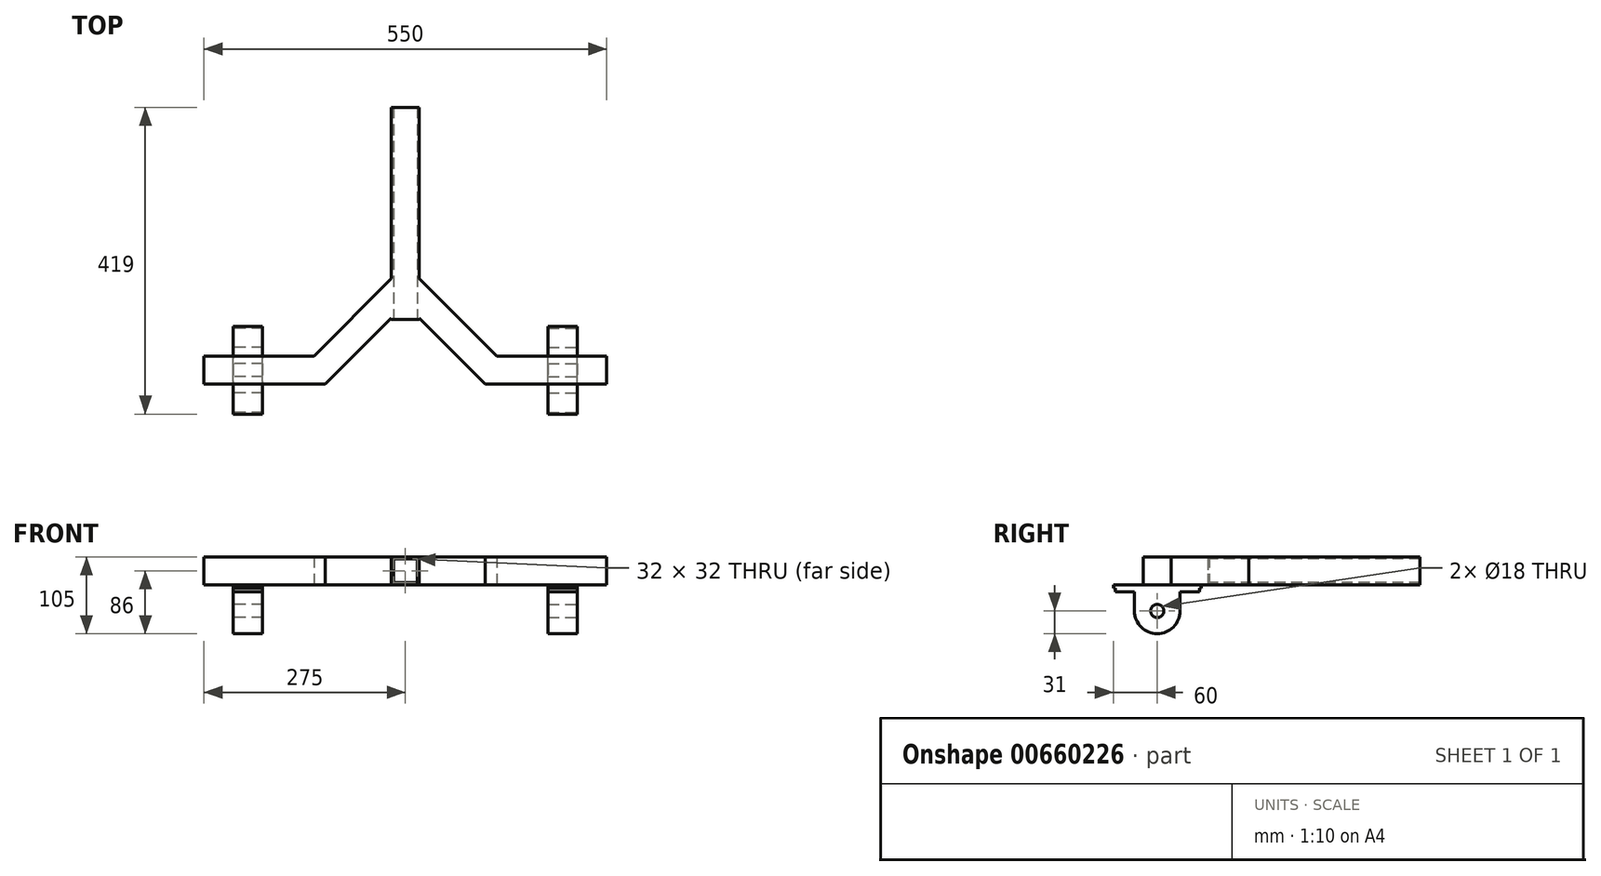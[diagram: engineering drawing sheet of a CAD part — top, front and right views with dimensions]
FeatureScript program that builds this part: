
annotation { "Feature Type Name" : "Feature", "Feature Type Description" : "" }
export const myFeature = defineFeature(function(context is Context, id is Id, definition is map)
    precondition{}
    {
        {
            var Q0;
            Q0=qCreatedBy(makeId("Top.planeOp"),FACE);
            var sketch = newSketch(context, id + "F0", { "sketchPlane" : qUnion([Q0])});
            skLineSegment(sketch, "E0.bottom", {"start": v(-275, -19) * mm, "end": v(-109.26, -19) * mm});
            skLineSegment(sketch, "E0.top", {"start": v(-275, 19) * mm, "end": v(-125, 19) * mm});
            skLineSegment(sketch, "E0.left", {"start": v(-275, -19) * mm, "end": v(-275, 19) * mm});
            skLineSegment(sketch, "E0.right", {"start": v(275, -19) * mm, "end": v(275, 19) * mm});
            skLineSegment(sketch, "E1", {"start": v(-125, 19) * mm, "end": v(-19, 125) * mm});
            skLineSegment(sketch, "E2", {"start": v(125, 19) * mm, "end": v(19, 125) * mm});
            skLineSegment(sketch, "E3", {"start": v(-109.26, -19) * mm, "end": v(-19, 71.26) * mm});
            skLineSegment(sketch, "E4.bottom", {"start": v(-19, 69) * mm, "end": v(19, 69) * mm});
            skLineSegment(sketch, "E4.top", {"start": v(-19, 359) * mm, "end": v(19, 359) * mm});
            skLineSegment(sketch, "E4.left", {"start": v(-19, 69) * mm, "end": v(-19, 71.26) * mm});
            skLineSegment(sketch, "E4.right", {"start": v(19, 69) * mm, "end": v(19, 71.26) * mm});
            skLineSegment(sketch, "E5.trimOffspring", {"start": v(109.26, -19) * mm, "end": v(275, -19) * mm});
            skLineSegment(sketch, "E6.trimOffspring", {"start": v(125, 19) * mm, "end": v(275, 19) * mm});
            skLineSegment(sketch, "E7.trimOffspring", {"start": v(-19, 125) * mm, "end": v(-19, 359) * mm});
            skLineSegment(sketch, "E8.trimOffspring", {"start": v(19, 71.26) * mm, "end": v(109.26, -19) * mm});
            skLineSegment(sketch, "E9.trimOffspring", {"start": v(19, 125) * mm, "end": v(19, 359) * mm});
            skSolve(sketch);
        }
        {
            var Q0;
            Q0 = qSketchRegion(id + "F0", true);
            extrude(context, id + "F1", {"entities" : qUnion([Q0]), "depth" : 38 * mm, "offsetDistance" : 25 * mm});
        }
        {
            var Q0;
            Q0=makeQuery(id+"F1.opExtrude","SWEPT_FACE",FACE,{"disambiguationData":[OSD([sQuery(id+"F0.wireOp",EDGE,"E4.bottom")])]});
            var sketch = newSketch(context, id + "F2", { "sketchPlane" : qUnion([Q0])});
            skLineSegment(sketch, "E10.bottom", {"start": v(-16, 35) * mm, "end": v(16, 35) * mm});
            skLineSegment(sketch, "E10.top", {"start": v(-16, 3) * mm, "end": v(16, 3) * mm});
            skLineSegment(sketch, "E10.left", {"start": v(-16, 35) * mm, "end": v(-16, 3) * mm});
            skLineSegment(sketch, "E10.right", {"start": v(16, 35) * mm, "end": v(16, 3) * mm});
            skSolve(sketch);
        }
        {
            var Q0;
            Q0 = qSketchRegion(id + "F2", true);
            extrude(context, id + "F3", {"entities" : qUnion([Q0]), "operationType" : NewBodyOperationType.REMOVE, "endBound" : BoundingType.THROUGH_ALL, "oppositeDirection" : true, "depth" : 150 * mm, "offsetDistance" : 25 * mm});
        }
        {
            var Q0;
            Q0=makeQuery(id+"F1.opExtrude","CAP_FACE",FACE,{"disambiguationData":[OSD([sQuery(id+"F0.wireOp",EDGE,"E0.bottom"),sQuery(id+"F0.wireOp",EDGE,"E0.top"),sQuery(id+"F0.wireOp",EDGE,"E0.left"),sQuery(id+"F0.wireOp",EDGE,"E0.right"),sQuery(id+"F0.wireOp",EDGE,"E1"),sQuery(id+"F0.wireOp",EDGE,"E2"),sQuery(id+"F0.wireOp",EDGE,"E3"),sQuery(id+"F0.wireOp",EDGE,"E4.bottom"),sQuery(id+"F0.wireOp",EDGE,"E4.top"),sQuery(id+"F0.wireOp",EDGE,"E4.left"),sQuery(id+"F0.wireOp",EDGE,"E4.right"),sQuery(id+"F0.wireOp",EDGE,"E5.trimOffspring"),sQuery(id+"F0.wireOp",EDGE,"E6.trimOffspring"),sQuery(id+"F0.wireOp",EDGE,"E7.trimOffspring"),sQuery(id+"F0.wireOp",EDGE,"E8.trimOffspring"),sQuery(id+"F0.wireOp",EDGE,"E9.trimOffspring")])],"isStart":true});
            var sketch = newSketch(context, id + "F4", { "sketchPlane" : qUnion([Q0])});
            skLineSegment(sketch, "E11.bottom", {"start": v(-235, 60) * mm, "end": v(-195, 60) * mm});
            skLineSegment(sketch, "E11.top", {"start": v(-235, -60) * mm, "end": v(-195, -60) * mm});
            skLineSegment(sketch, "E11.left", {"start": v(-235, 60) * mm, "end": v(-235, -60) * mm});
            skLineSegment(sketch, "E11.right", {"start": v(-195, 60) * mm, "end": v(-195, -60) * mm});
            skLineSegment(sketch, "E12.bottom", {"start": v(195, 60) * mm, "end": v(235, 60) * mm});
            skLineSegment(sketch, "E12.top", {"start": v(195, -60) * mm, "end": v(235, -60) * mm});
            skLineSegment(sketch, "E12.left", {"start": v(195, 60) * mm, "end": v(195, -60) * mm});
            skLineSegment(sketch, "E12.right", {"start": v(235, 60) * mm, "end": v(235, -60) * mm});
            skSolve(sketch);
        }
        {
            var Q0;
            Q0 = qSketchRegion(id + "F4", true);
            extrude(context, id + "F5", {"entities" : qUnion([Q0]), "operationType" : NewBodyOperationType.ADD, "depth" : 5 * mm, "offsetDistance" : 25 * mm});
        }
        {
            var Q0;
            Q0=makeQuery(id+"F5.opExtrude","SWEPT_FACE",FACE,{"disambiguationData":[OSD([sQuery(id+"F4.wireOp",EDGE,"E11.left")])]});
            var sketch = newSketch(context, id + "F6", { "sketchPlane" : qUnion([Q0])});
            skCircle(sketch, "E13", {"center": v(0, -36) * mm, "radius": 9 * mm});
            skArc(sketch, "E14", {"start": v(-31, -36) * mm, "mid": v(0, -67) * mm, "end": v(31, -36) * mm});
            skLineSegment(sketch, "E15.bottom", {"start": v(-57.5, -5) * mm, "end": v(57.5, -5) * mm});
            skLineSegment(sketch, "E15.top", {"start": v(-57.5, -10) * mm, "end": v(-31, -10) * mm});
            skLineSegment(sketch, "E15.left", {"start": v(-57.5, -5) * mm, "end": v(-57.5, -10) * mm});
            skLineSegment(sketch, "E15.right", {"start": v(57.5, -5) * mm, "end": v(57.5, -10) * mm});
            skLineSegment(sketch, "E16.left", {"start": v(-31, -10) * mm, "end": v(-31, -36) * mm});
            skLineSegment(sketch, "E16.right", {"start": v(31, -10) * mm, "end": v(31, -36) * mm});
            skLineSegment(sketch, "E17.trimOffspring", {"start": v(31, -10) * mm, "end": v(57.5, -10) * mm});
            skSolve(sketch);
        }
        {
            var Q0;
            Q0=makeQuery(id+"F6.imprint","IMPRINT",FACE,{"disambiguationData":[TD([[makeQuery(id+"F6.imprint","IMPRINT",EDGE,{"derivedFrom":sQuery(id+"F6.wireOp",EDGE,"E13")}),-1.0]])]});
            extrude(context, id + "F7", {"entities" : qUnion([Q0]), "operationType" : NewBodyOperationType.ADD, "oppositeDirection" : true, "depth" : 40 * mm, "offsetDistance" : 25 * mm});
        }
        {
            var Q0;
            Q0=makeQuery(id+"F5.opExtrude","SWEPT_FACE",FACE,{"disambiguationData":[OSD([sQuery(id+"F4.wireOp",EDGE,"E12.right")])]});
            var sketch = newSketch(context, id + "F8", { "sketchPlane" : qUnion([Q0])});
            skCircle(sketch, "E18", {"center": v(0, -36) * mm, "radius": 9 * mm});
            skArc(sketch, "E19", {"start": v(-31, -36) * mm, "mid": v(0, -67) * mm, "end": v(31, -36) * mm});
            skLineSegment(sketch, "E20.bottom", {"start": v(-57.5, -5) * mm, "end": v(57.5, -5) * mm});
            skLineSegment(sketch, "E20.top", {"start": v(-57.5, -10) * mm, "end": v(-31, -10) * mm});
            skLineSegment(sketch, "E20.left", {"start": v(-57.5, -5) * mm, "end": v(-57.5, -10) * mm});
            skLineSegment(sketch, "E20.right", {"start": v(57.5, -5) * mm, "end": v(57.5, -10) * mm});
            skLineSegment(sketch, "E21.left", {"start": v(-31, -10) * mm, "end": v(-31, -36) * mm});
            skLineSegment(sketch, "E21.right", {"start": v(31, -10) * mm, "end": v(31, -36) * mm});
            skLineSegment(sketch, "E22.trimOffspring", {"start": v(31, -10) * mm, "end": v(57.5, -10) * mm});
            skSolve(sketch);
        }
        {
            var Q0;
            Q0=makeQuery(id+"F8.imprint","IMPRINT",FACE,{"disambiguationData":[TD([[makeQuery(id+"F8.imprint","IMPRINT",EDGE,{"derivedFrom":sQuery(id+"F8.wireOp",EDGE,"E18")}),-1.0]])]});
            extrude(context, id + "F9", {"entities" : qUnion([Q0]), "operationType" : NewBodyOperationType.ADD, "oppositeDirection" : true, "depth" : 40 * mm, "offsetDistance" : 25 * mm});
        }
    });
